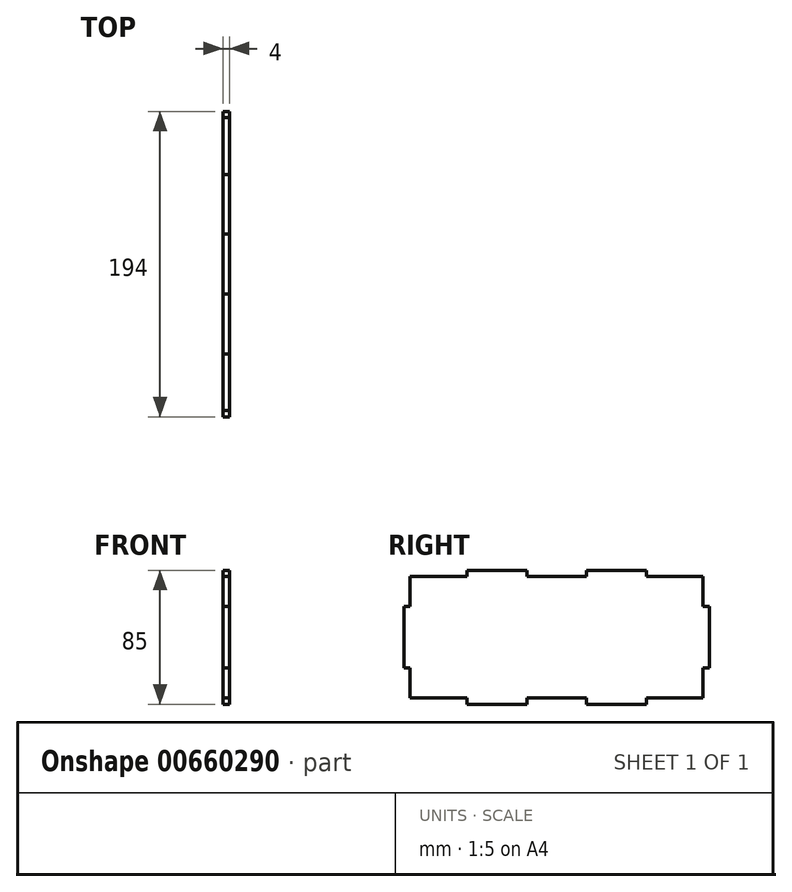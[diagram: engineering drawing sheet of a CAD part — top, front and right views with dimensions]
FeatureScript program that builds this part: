
annotation { "Feature Type Name" : "Feature", "Feature Type Description" : "" }
export const myFeature = defineFeature(function(context is Context, id is Id, definition is map)
    precondition{}
    {
        {
            var Q0;
            Q0=qCreatedBy(makeId("Right.planeOp"),FACE);
            var sketch = newSketch(context, id + "F0", { "sketchPlane" : qUnion([Q0])});
            skLineSegment(sketch, "E0.bottom", {"start": v(0, 0) * mm, "end": v(194, 0) * mm});
            skLineSegment(sketch, "E0.top", {"start": v(0, 85) * mm, "end": v(194, 85) * mm});
            skLineSegment(sketch, "E0.left", {"start": v(0, 0) * mm, "end": v(0, 85) * mm});
            skLineSegment(sketch, "E0.right", {"start": v(194, 0) * mm, "end": v(194, 85) * mm});
            skLineSegment(sketch, "E1.bottom", {"start": v(0, 85) * mm, "end": v(4, 85) * mm});
            skLineSegment(sketch, "E1.top", {"start": v(0, 62) * mm, "end": v(4, 62) * mm});
            skLineSegment(sketch, "E1.left", {"start": v(0, 85) * mm, "end": v(0, 62) * mm});
            skLineSegment(sketch, "E1.right", {"start": v(4, 85) * mm, "end": v(4, 62) * mm});
            skLineSegment(sketch, "E2.bottom", {"start": v(0, 0) * mm, "end": v(4, 0) * mm});
            skLineSegment(sketch, "E2.top", {"start": v(0, 23) * mm, "end": v(4, 23) * mm});
            skLineSegment(sketch, "E2.left", {"start": v(0, 0) * mm, "end": v(0, 23) * mm});
            skLineSegment(sketch, "E2.right", {"start": v(4, 0) * mm, "end": v(4, 23) * mm});
            skLineSegment(sketch, "E3.bottom", {"start": v(194, 85) * mm, "end": v(190, 85) * mm});
            skLineSegment(sketch, "E3.top", {"start": v(194, 62) * mm, "end": v(190, 62) * mm});
            skLineSegment(sketch, "E3.left", {"start": v(194, 85) * mm, "end": v(194, 62) * mm});
            skLineSegment(sketch, "E3.right", {"start": v(190, 85) * mm, "end": v(190, 62) * mm});
            skLineSegment(sketch, "E4.bottom", {"start": v(194, 0) * mm, "end": v(190, 0) * mm});
            skLineSegment(sketch, "E4.top", {"start": v(194, 23) * mm, "end": v(190, 23) * mm});
            skLineSegment(sketch, "E4.left", {"start": v(194, 0) * mm, "end": v(194, 23) * mm});
            skLineSegment(sketch, "E4.right", {"start": v(190, 0) * mm, "end": v(190, 23) * mm});
            skLineSegment(sketch, "E5.bottom", {"start": v(0, 0) * mm, "end": v(40, 0) * mm});
            skLineSegment(sketch, "E5.top", {"start": v(0, 4) * mm, "end": v(40, 4) * mm});
            skLineSegment(sketch, "E5.left", {"start": v(0, 0) * mm, "end": v(0, 4) * mm});
            skLineSegment(sketch, "E5.right", {"start": v(40, 0) * mm, "end": v(40, 4) * mm});
            skLineSegment(sketch, "E6.bottom", {"start": v(78, 0) * mm, "end": v(116, 0) * mm});
            skLineSegment(sketch, "E6.top", {"start": v(78, 4) * mm, "end": v(116, 4) * mm});
            skLineSegment(sketch, "E6.left", {"start": v(78, 0) * mm, "end": v(78, 4) * mm});
            skLineSegment(sketch, "E6.right", {"start": v(116, 0) * mm, "end": v(116, 4) * mm});
            skLineSegment(sketch, "E7.bottom", {"start": v(194, 0) * mm, "end": v(154, 0) * mm});
            skLineSegment(sketch, "E7.top", {"start": v(194, 4) * mm, "end": v(154, 4) * mm});
            skLineSegment(sketch, "E7.left", {"start": v(194, 0) * mm, "end": v(194, 4) * mm});
            skLineSegment(sketch, "E7.right", {"start": v(154, 0) * mm, "end": v(154, 4) * mm});
            skLineSegment(sketch, "E8.bottom", {"start": v(194, 85) * mm, "end": v(154, 85) * mm});
            skLineSegment(sketch, "E8.top", {"start": v(194, 81) * mm, "end": v(154, 81) * mm});
            skLineSegment(sketch, "E8.left", {"start": v(194, 85) * mm, "end": v(194, 81) * mm});
            skLineSegment(sketch, "E8.right", {"start": v(154, 85) * mm, "end": v(154, 81) * mm});
            skLineSegment(sketch, "E9.bottom", {"start": v(116, 85) * mm, "end": v(78, 85) * mm});
            skLineSegment(sketch, "E9.top", {"start": v(116, 81) * mm, "end": v(78, 81) * mm});
            skLineSegment(sketch, "E9.left", {"start": v(116, 85) * mm, "end": v(116, 81) * mm});
            skLineSegment(sketch, "E9.right", {"start": v(78, 85) * mm, "end": v(78, 81) * mm});
            skLineSegment(sketch, "E10.bottom", {"start": v(0, 85) * mm, "end": v(40, 85) * mm});
            skLineSegment(sketch, "E10.top", {"start": v(0, 81) * mm, "end": v(40, 81) * mm});
            skLineSegment(sketch, "E10.left", {"start": v(0, 85) * mm, "end": v(0, 81) * mm});
            skLineSegment(sketch, "E10.right", {"start": v(40, 85) * mm, "end": v(40, 81) * mm});
            skSolve(sketch);
        }
        {
            var Q0;
            {var subQ20=sQuery(id+"F0.wireOp",EDGE,"E1.top");Q0=makeQuery(id+"F0.imprint","IMPRINT",FACE,{"disambiguationData":[TD([[makeQuery(id+"F0.imprint","IMPRINT",EDGE,{"derivedFrom":subQ20}),-1.0]])]});}
            extrude(context, id + "F1", {"entities" : qUnion([Q0]), "depth" : 4 * mm, "offsetDistance" : 25 * mm});
        }
    });
